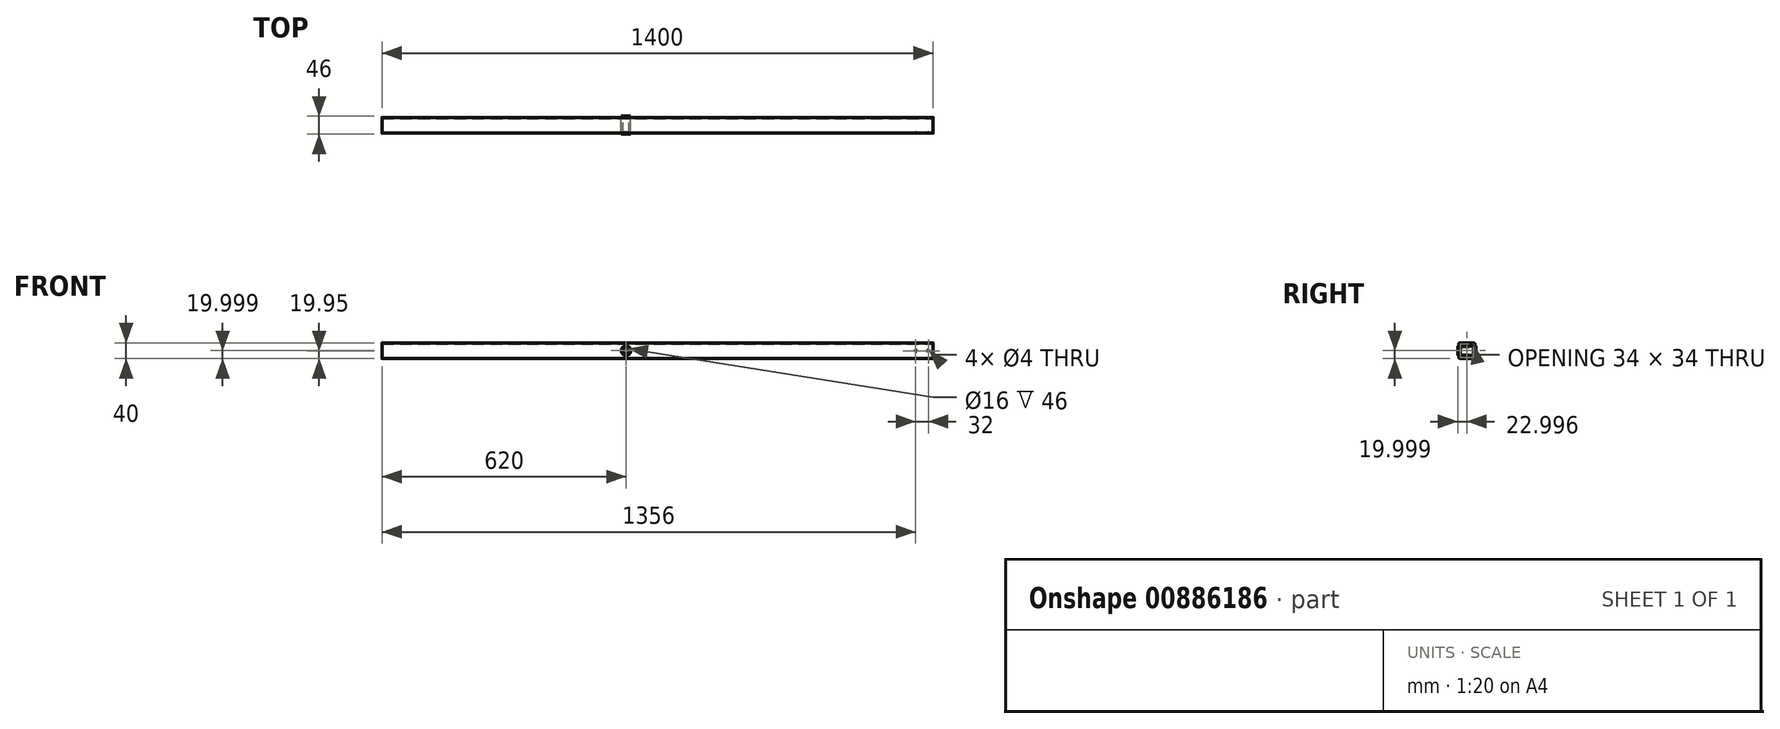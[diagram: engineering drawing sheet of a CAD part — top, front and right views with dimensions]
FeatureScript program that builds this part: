
annotation { "Feature Type Name" : "Feature", "Feature Type Description" : "" }
export const myFeature = defineFeature(function(context is Context, id is Id, definition is map)
    precondition{}
    {
        {
            assignVariable(context, id + "F0", {"name" : "spanntraeger", "anyValue" : 1400});
        }
        {
            assignVariable(context, id + "F1", {"name" : "HaupttraegerRohr_X", "anyValue" : 40});
        }
        {
            var Q0;
            Q0=qCreatedBy(makeId("Right.planeOp"),FACE);
            var sketch = newSketch(context, id + "F2", { "sketchPlane" : qUnion([Q0])});
            skLineSegment(sketch, "E0.bottom", {"start": v(-17.11, 20.05) * mm, "end": v(18.89, 20.05) * mm});
            skLineSegment(sketch, "E0.top", {"start": v(-17.11, -19.95) * mm, "end": v(18.89, -19.95) * mm});
            skLineSegment(sketch, "E0.left", {"start": v(-19.11, 18.05) * mm, "end": v(-19.11, -17.95) * mm});
            skLineSegment(sketch, "E0.right", {"start": v(20.89, 18.05) * mm, "end": v(20.89, -17.95) * mm});
            skLineSegment(sketch, "E1.0", {"start": v(-16.11, 15.05) * mm, "end": v(-16.11, -14.95) * mm});
            skLineSegment(sketch, "E1.1", {"start": v(-14.11, 17.05) * mm, "end": v(17.89, 17.05) * mm});
            skLineSegment(sketch, "E1.2", {"start": v(17.89, 17.05) * mm, "end": v(17.89, -14.95) * mm});
            skLineSegment(sketch, "E1.3", {"start": v(-14.11, -16.95) * mm, "end": v(15.89, -16.95) * mm});
            skPoint(sketch, "E2.visualSharp", {"position": v(-19.11, 20.05) * mm});
            skArc(sketch, "E2.filletArc", {"start": v(-17.11, 20.05) * mm, "mid": v(-18.53, 19.46) * mm, "end": v(-19.11, 18.05) * mm});
            skPoint(sketch, "E3.visualSharp", {"position": v(-19.11, -19.95) * mm});
            skArc(sketch, "E3.filletArc", {"start": v(-19.11, -17.95) * mm, "mid": v(-18.53, -19.36) * mm, "end": v(-17.11, -19.95) * mm});
            skPoint(sketch, "E4.visualSharp", {"position": v(20.89, -19.95) * mm});
            skArc(sketch, "E4.filletArc", {"start": v(18.89, -19.95) * mm, "mid": v(20.3, -19.36) * mm, "end": v(20.89, -17.95) * mm});
            skPoint(sketch, "E5.visualSharp", {"position": v(20.89, 20.05) * mm});
            skArc(sketch, "E5.filletArc", {"start": v(20.89, 18.05) * mm, "mid": v(20.3, 19.46) * mm, "end": v(18.89, 20.05) * mm});
            skPoint(sketch, "E6.visualSharp", {"position": v(17.89, -16.95) * mm});
            skArc(sketch, "E6.filletArc", {"start": v(15.89, -16.95) * mm, "mid": v(17.3, -16.36) * mm, "end": v(17.89, -14.95) * mm});
            skPoint(sketch, "E7.visualSharp", {"position": v(-16.11, -16.95) * mm});
            skArc(sketch, "E7.filletArc", {"start": v(-16.11, -14.95) * mm, "mid": v(-15.53, -16.36) * mm, "end": v(-14.11, -16.95) * mm});
            skPoint(sketch, "E8.visualSharp", {"position": v(-16.11, 17.05) * mm});
            skArc(sketch, "E8.filletArc", {"start": v(-14.11, 17.05) * mm, "mid": v(-15.53, 16.46) * mm, "end": v(-16.11, 15.05) * mm});
            skSolve(sketch);
        }
        {
            var Q0;
            Q0 = qSketchRegion(id + "F2", true);
            extrude(context, id + "F3", {"entities" : qUnion([Q0]), "oppositeDirection" : true, "depth" : (getVariable(context, 'spanntraeger')) * mm, "offsetDistance" : 25 * mm});
        }
        {
            var Q0;
            Q0=makeQuery(id+"F3.opExtrude","SWEPT_FACE",FACE,{"disambiguationData":[OSD([sQuery(id+"F2.wireOp",EDGE,"E0.left")])]});
            var sketch = newSketch(context, id + "F4", { "sketchPlane" : qUnion([Q0])});
            skCircle(sketch, "E9", {"center": v(-780, 0.05) * mm, "radius": 8 * mm});
            skCircle(sketch, "E10", {"center": v(-780, 0.05) * mm, "radius": 12 * mm});
            skLineSegment(sketch, "E11", {"start": v(0, 0) * mm, "end": v(-110.05, 0) * mm, "construction": true});
            skCircle(sketch, "E12", {"center": v(-12, 0) * mm, "radius": 2 * mm});
            skCircle(sketch, "E13", {"center": v(-44, 0) * mm, "radius": 2 * mm});
            skSolve(sketch);
        }
        {
            var Q0;
            Q0=makeQuery(id+"F4.imprint","IMPRINT",FACE,{"disambiguationData":[TD([[makeQuery(id+"F4.imprint","IMPRINT",EDGE,{"derivedFrom":sQuery(id+"F4.wireOp",EDGE,"E9")}),-1.0]])]});
            extrude(context, id + "F5", {"entities" : qUnion([Q0]), "operationType" : NewBodyOperationType.ADD, "depth" : 3 * mm, "offsetDistance" : 25 * mm, "hasSecondDirection" : true, "secondDirectionOppositeDirection" : true, "secondDirectionDepth" : (getVariable(context, 'HaupttraegerRohr_X') + 3) * mm});
        }
        {
            var Q0;
            Q0=makeQuery(id+"F5.boolean.opBoolean","SPLIT",FACE,{"disambiguationData":[TD([makeQuery(id+"F5.opExtrude","SWEPT_FACE",FACE,{"disambiguationData":[OSD([sQuery(id+"F4.wireOp",EDGE,"E9")])]})])],"derivedFrom":makeQuery(id+"F3.opExtrude","SWEPT_FACE",FACE,{"disambiguationData":[OSD([sQuery(id+"F2.wireOp",EDGE,"E0.right")])]})});
            extrude(context, id + "F6", {"entities" : qUnion([Q0]), "operationType" : NewBodyOperationType.REMOVE, "oppositeDirection" : true, "depth" : 63 * mm, "offsetDistance" : 25 * mm});
        }
        {
            var Q0;
            Q0=makeQuery(id+"F4.imprint","IMPRINT",FACE,{"disambiguationData":[TD([[makeQuery(id+"F4.imprint","IMPRINT",EDGE,{"derivedFrom":sQuery(id+"F4.wireOp",EDGE,"E13")}),1.0]])]});
            var Q1;
            Q1=makeQuery(id+"F4.imprint","IMPRINT",FACE,{"disambiguationData":[TD([[makeQuery(id+"F4.imprint","IMPRINT",EDGE,{"derivedFrom":sQuery(id+"F4.wireOp",EDGE,"E12")}),1.0]])]});
            extrude(context, id + "F7", {"entities" : qUnion([Q0, Q1]), "operationType" : NewBodyOperationType.REMOVE, "oppositeDirection" : true, "depth" : 50000 * mm, "offsetDistance" : 25 * mm});
        }
    });
